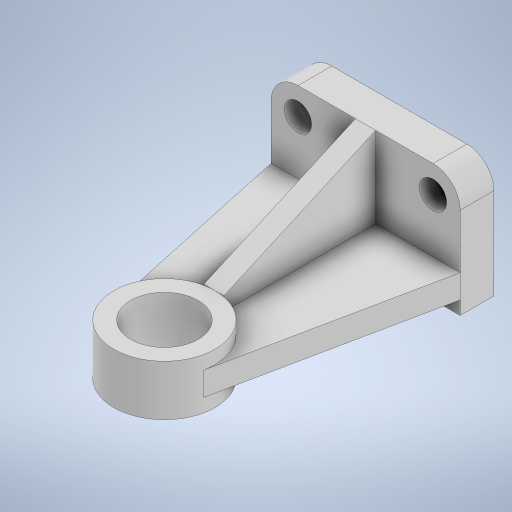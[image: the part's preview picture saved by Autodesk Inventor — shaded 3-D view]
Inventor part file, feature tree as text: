
AUTODESK INVENTOR PART (.ipt)
format: ipt  version: 2024 (Build 280153000, 153)  size: 293,888 bytes
history: native  units: mm
features: extrude x5, sketch x3, other x1, plane x1
ambient origin geometry x8: Origin, YZ Plane, XZ Plane, XY Plane, X Axis, Y Axis, Z Axis, Center Point
bodies: Body1 (feature_tree)
feature tree (10):
  other  "Sólido1"
  extrude  "Extrusión1"  Depth=35.0mm
  plane  "Plano de trabajo2"
  sketch  "Boceto2"  dims[d2=8.0mm d3=8.0mm]
  extrude  "Extrusión2"  Depth=8.0mm
  extrude  "Extrusión3"  Depth=10.0mm TaperAngle=0.0deg
  extrude  "Extrusión4"  [1 undecoded]
  extrude  "Extrusión5"  Depth=6.0mm
  sketch  "Boceto1"  dims[d0=56.0mm d1=35.0mm]
  sketch  "Boceto3"  dims[d4=8.0mm d5=10.0mm d6=0.0mm d7=-4.0mm d8=30.0mm d9=20.0mm d11=7.0mm d12=0.0mm d13=11.0mm d14=0.0mm d15=4.0mm d16=0.0mm d17=24.0mm d18=6.0mm d19=0.0mm d20=0.5mm d21=0.872665mm]
note: 1 required parameter value undecoded (feature->parameter linkage not recoverable at this tier; creation-order binding heuristic only, values carry confidence <= 0.55)
